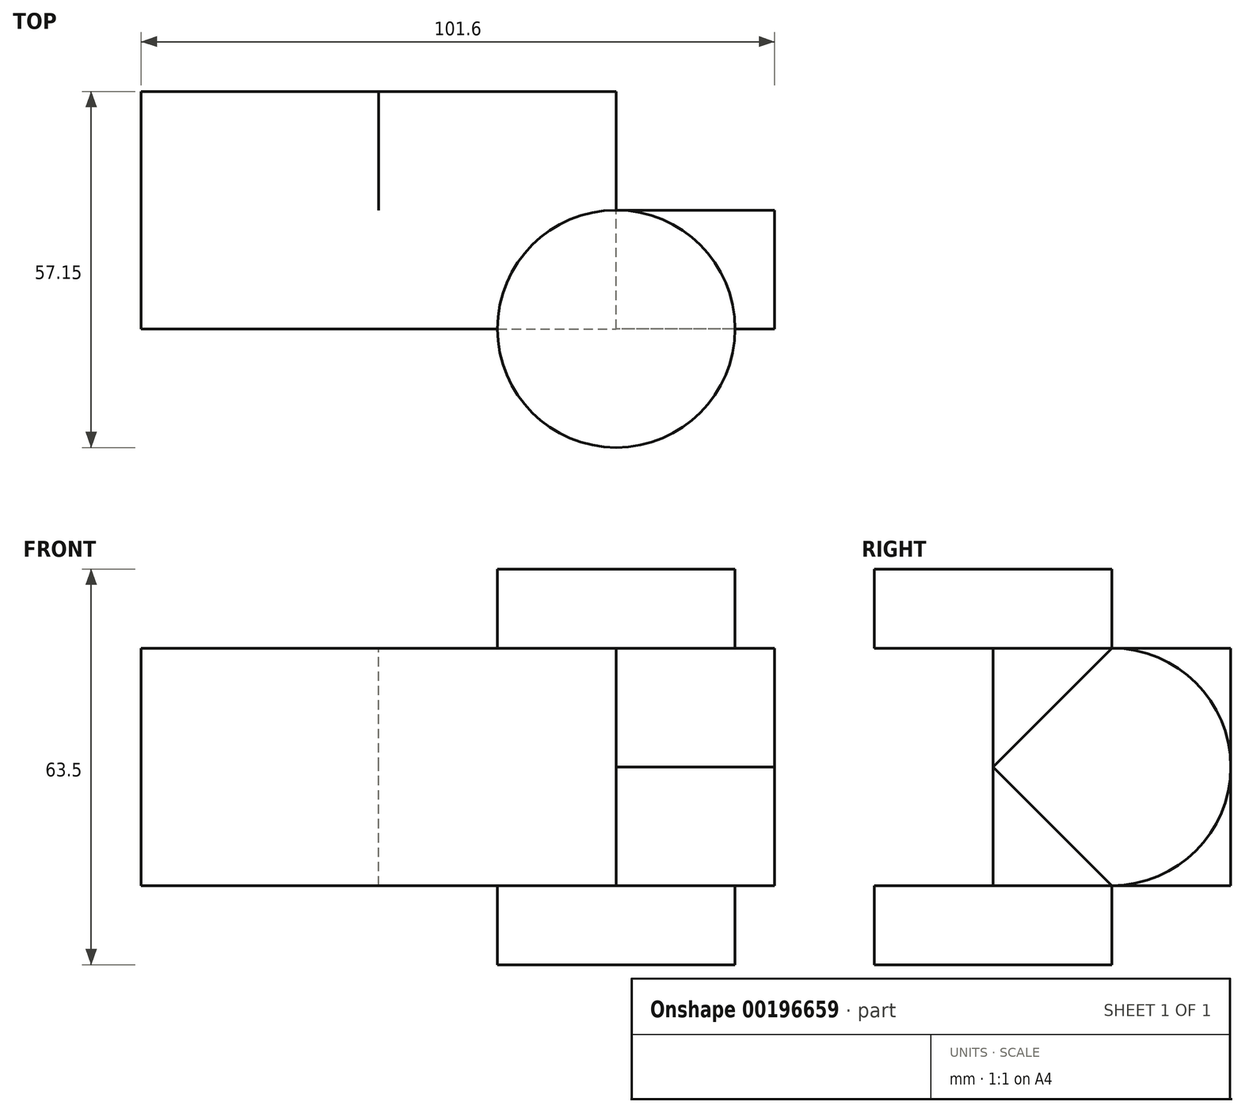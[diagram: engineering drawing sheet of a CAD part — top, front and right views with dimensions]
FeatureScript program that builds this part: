
annotation { "Feature Type Name" : "Feature", "Feature Type Description" : "" }
export const myFeature = defineFeature(function(context is Context, id is Id, definition is map)
    precondition{}
    {
        {
            var Q0;
            Q0=qCreatedBy(makeId("Front.planeOp"),FACE);
            var sketch = newSketch(context, id + "F0", { "sketchPlane" : qUnion([Q0])});
            skLineSegment(sketch, "E0.bottom", {"start": v(-64.64, -24.87) * mm, "end": v(-26.54, -24.87) * mm});
            skLineSegment(sketch, "E0.top", {"start": v(-64.64, 13.23) * mm, "end": v(-26.54, 13.23) * mm});
            skLineSegment(sketch, "E0.left", {"start": v(-64.64, -24.87) * mm, "end": v(-64.64, 13.23) * mm});
            skLineSegment(sketch, "E0.right", {"start": v(-26.54, -24.87) * mm, "end": v(-26.54, 13.23) * mm});
            skSolve(sketch);
        }
        {
            var Q0;
            Q0=makeQuery(id+"F0.imprint","IMPRINT",FACE,{"disambiguationData":[TD([[makeQuery(id+"F0.imprint","IMPRINT",EDGE,{"derivedFrom":sQuery(id+"F0.wireOp",EDGE,"E0.bottom")}),1.0]])]});
            extrude(context, id + "F1", {"entities" : qUnion([Q0]), "depth" : 38.1 * mm});
        }
        {
            var Q0;
            Q0=makeQuery(id+"F1.opExtrude","SWEPT_FACE",FACE,{"disambiguationData":[OSD([sQuery(id+"F0.wireOp",EDGE,"E0.right")])]});
            var sketch = newSketch(context, id + "F2", { "sketchPlane" : qUnion([Q0])});
            skLineSegment(sketch, "E1", {"start": v(-19.05, -24.87) * mm, "end": v(-19.05, 13.23) * mm});
            skCircle(sketch, "E2", {"center": v(-19.05, -5.82) * mm, "radius": 19.05 * mm});
            skSolve(sketch);
        }
        {
            var Q0;
            {var subQ0=sQuery(id+"F2.wireOp",EDGE,"E1");Q0=makeQuery(id+"F2.imprint","IMPRINT",FACE,{"disambiguationData":[TD([[makeQuery(id+"F2.imprint","IMPRINT",EDGE,{"derivedFrom":subQ0}),-1.0]])]});}
            extrude(context, id + "F3", {"entities" : qUnion([Q0]), "operationType" : NewBodyOperationType.ADD, "depth" : 38.1 * mm});
        }
        {
            var Q0;
            Q0=makeQuery(id+"F3.opExtrude","SWEPT_FACE",FACE,{"disambiguationData":[OSD([sQuery(id+"F2.wireOp",EDGE,"E1")])]});
            extrude(context, id + "F4", {"entities" : qUnion([Q0]), "operationType" : NewBodyOperationType.ADD, "depth" : 19.05 * mm});
        }
        {
            var Q0;
            {var subQ0=sQuery(id+"F0.wireOp",EDGE,"E0.bottom");Q0=makeQuery(id+"F4.boolean.opBoolean","MERGE",FACE,{"derivedFrom":[makeQuery(id+"F1.opExtrude","SWEPT_FACE",FACE,{"disambiguationData":[OSD([subQ0])]}),makeQuery(id+"F4.opExtrude","SWEPT_FACE",FACE,{"disambiguationData":[OSD([subQ0,sQuery(id+"F0.wireOp",EDGE,"E0.right"),sQuery(id+"F2.wireOp",EDGE,"E1"),sQuery(id+"F2.wireOp",EDGE,"E2")])]})]});}
            var sketch = newSketch(context, id + "F5", { "sketchPlane" : qUnion([Q0])});
            skCircle(sketch, "E3", {"center": v(11.56, 38.1) * mm, "radius": 19.05 * mm});
            skSolve(sketch);
        }
        {
            var Q0;
            {var subQ0=sQuery(id+"F0.wireOp",EDGE,"E0.top");Q0=makeQuery(id+"F4.boolean.opBoolean","MERGE",FACE,{"derivedFrom":[makeQuery(id+"F1.opExtrude","SWEPT_FACE",FACE,{"disambiguationData":[OSD([subQ0])]}),makeQuery(id+"F4.opExtrude","SWEPT_FACE",FACE,{"disambiguationData":[OSD([subQ0,sQuery(id+"F0.wireOp",EDGE,"E0.right"),sQuery(id+"F2.wireOp",EDGE,"E1"),sQuery(id+"F2.wireOp",EDGE,"E2")])]})]});}
            var sketch = newSketch(context, id + "F6", { "sketchPlane" : qUnion([Q0])});
            skCircle(sketch, "E4", {"center": v(11.56, -38.1) * mm, "radius": 19.05 * mm});
            skSolve(sketch);
        }
        {
            var Q0;
            {var subQ1=sQuery(id+"F2.wireOp",EDGE,"E2");var subQ2=sQuery(id+"F2.wireOp",EDGE,"E1");var subQ3=sQuery(id+"F0.wireOp",EDGE,"E0.right");var subQ4=sQuery(id+"F0.wireOp",EDGE,"E0.top");var subQ5=makeQuery(id+"F4.opExtrude","SWEPT_EDGE",EDGE,{"disambiguationData":[OSD([subQ4,subQ3,subQ2,subQ1]),TDD([makeQuery(id+"F3.opExtrude","CAP_VERTEX",VERTEX,{"disambiguationData":[OSD([subQ4,subQ3,subQ2,subQ1])],"isStart":false})])]});Q0=makeQuery(id+"F6.imprint","IMPRINT",FACE,{"disambiguationData":[TD([[makeQuery(id+"F6.imprint","IMPRINT",EDGE,{"derivedFrom":subQ5}),-1.0]])]});}
            var Q1;
            {var subQ1=sQuery(id+"F2.wireOp",EDGE,"E2");var subQ2=sQuery(id+"F2.wireOp",EDGE,"E1");var subQ3=sQuery(id+"F0.wireOp",EDGE,"E0.right");var subQ4=sQuery(id+"F0.wireOp",EDGE,"E0.top");var subQ5=makeQuery(id+"F4.opExtrude","SWEPT_EDGE",EDGE,{"disambiguationData":[OSD([subQ4,subQ3,subQ2,subQ1]),TDD([makeQuery(id+"F3.opExtrude","CAP_VERTEX",VERTEX,{"disambiguationData":[OSD([subQ4,subQ3,subQ2,subQ1])],"isStart":false})])]});Q1=makeQuery(id+"F6.imprint","IMPRINT",FACE,{"disambiguationData":[TD([[makeQuery(id+"F6.imprint","IMPRINT",EDGE,{"derivedFrom":subQ5}),1.0]])]});}
            extrude(context, id + "F7", {"entities" : qUnion([Q0, Q1]), "operationType" : NewBodyOperationType.ADD, "depth" : 12.7 * mm});
        }
        {
            var Q0;
            {var subQ1=sQuery(id+"F2.wireOp",EDGE,"E2");var subQ2=sQuery(id+"F2.wireOp",EDGE,"E1");var subQ3=sQuery(id+"F0.wireOp",EDGE,"E0.right");var subQ4=sQuery(id+"F0.wireOp",EDGE,"E0.bottom");var subQ5=makeQuery(id+"F4.opExtrude","SWEPT_EDGE",EDGE,{"disambiguationData":[OSD([subQ4,subQ3,subQ2,subQ1]),TDD([makeQuery(id+"F3.opExtrude","CAP_VERTEX",VERTEX,{"disambiguationData":[OSD([subQ4,subQ3,subQ2,subQ1])],"isStart":false})])]});Q0=makeQuery(id+"F5.imprint","IMPRINT",FACE,{"disambiguationData":[TD([[makeQuery(id+"F5.imprint","IMPRINT",EDGE,{"derivedFrom":subQ5}),1.0]])]});}
            var Q1;
            {var subQ1=sQuery(id+"F2.wireOp",EDGE,"E2");var subQ2=sQuery(id+"F2.wireOp",EDGE,"E1");var subQ3=sQuery(id+"F0.wireOp",EDGE,"E0.right");var subQ4=sQuery(id+"F0.wireOp",EDGE,"E0.bottom");var subQ5=makeQuery(id+"F4.opExtrude","SWEPT_EDGE",EDGE,{"disambiguationData":[OSD([subQ4,subQ3,subQ2,subQ1]),TDD([makeQuery(id+"F3.opExtrude","CAP_VERTEX",VERTEX,{"disambiguationData":[OSD([subQ4,subQ3,subQ2,subQ1])],"isStart":false})])]});Q1=makeQuery(id+"F5.imprint","IMPRINT",FACE,{"disambiguationData":[TD([[makeQuery(id+"F5.imprint","IMPRINT",EDGE,{"derivedFrom":subQ5}),-1.0]])]});}
            extrude(context, id + "F8", {"entities" : qUnion([Q0, Q1]), "operationType" : NewBodyOperationType.ADD, "depth" : 12.7 * mm});
        }
        {
            var Q0;
            {var subQ0=sQuery(id+"F2.wireOp",EDGE,"E1");Q0=makeQuery(id+"F4.boolean.opBoolean","MERGE",FACE,{"derivedFrom":[makeQuery(id+"F3.opExtrude","CAP_FACE",FACE,{"disambiguationData":[OSD([subQ0,sQuery(id+"F2.wireOp",EDGE,"E2")])],"isStart":false}),makeQuery(id+"F4.opExtrude","SWEPT_FACE",FACE,{"disambiguationData":[OSD([subQ0]),TDD([makeQuery(id+"F3.opExtrude","CAP_EDGE",EDGE,{"disambiguationData":[OSD([subQ0])],"isStart":false})])]})]});}
            var sketch = newSketch(context, id + "F9", { "sketchPlane" : qUnion([Q0])});
            skLineSegment(sketch, "E5", {"start": v(-38.1, -5.82) * mm, "end": v(-19.05, 13.23) * mm});
            skLineSegment(sketch, "E6", {"start": v(-19.05, 13.23) * mm, "end": v(-19.05, -24.87) * mm});
            skLineSegment(sketch, "E7", {"start": v(-19.05, -24.87) * mm, "end": v(-38.1, -5.82) * mm});
            skSolve(sketch);
        }
        {
            var Q0;
            {var subQ0=sQuery(id+"F9.wireOp",EDGE,"E7");Q0=makeQuery(id+"F9.imprint","IMPRINT",FACE,{"disambiguationData":[TD([[makeQuery(id+"F9.imprint","IMPRINT",EDGE,{"derivedFrom":subQ0}),1.0]])]});}
            var sketch = newSketch(context, id + "F10", { "sketchPlane" : qUnion([Q0])});
            skSolve(sketch);
        }
        {
            var Q0;
            {var subQ0=sQuery(id+"F9.wireOp",EDGE,"E7");Q0=makeQuery(id+"F10.imprint","IMPRINT",FACE,{"disambiguationData":[TD([[makeQuery(id+"F10.imprint","IMPRINT",EDGE,{"derivedFrom":makeQuery(id+"F9.imprint","IMPRINT",EDGE,{"derivedFrom":subQ0})}),1.0]])]});}
            var Q1;
            {var subQ0=sQuery(id+"F9.wireOp",EDGE,"E5");Q1=makeQuery(id+"F9.imprint","IMPRINT",FACE,{"disambiguationData":[TD([[makeQuery(id+"F9.imprint","IMPRINT",EDGE,{"derivedFrom":subQ0}),1.0]])]});}
            extrude(context, id + "F11", {"entities" : qUnion([Q0, Q1]), "depth" : 25.4 * mm});
        }
    });
